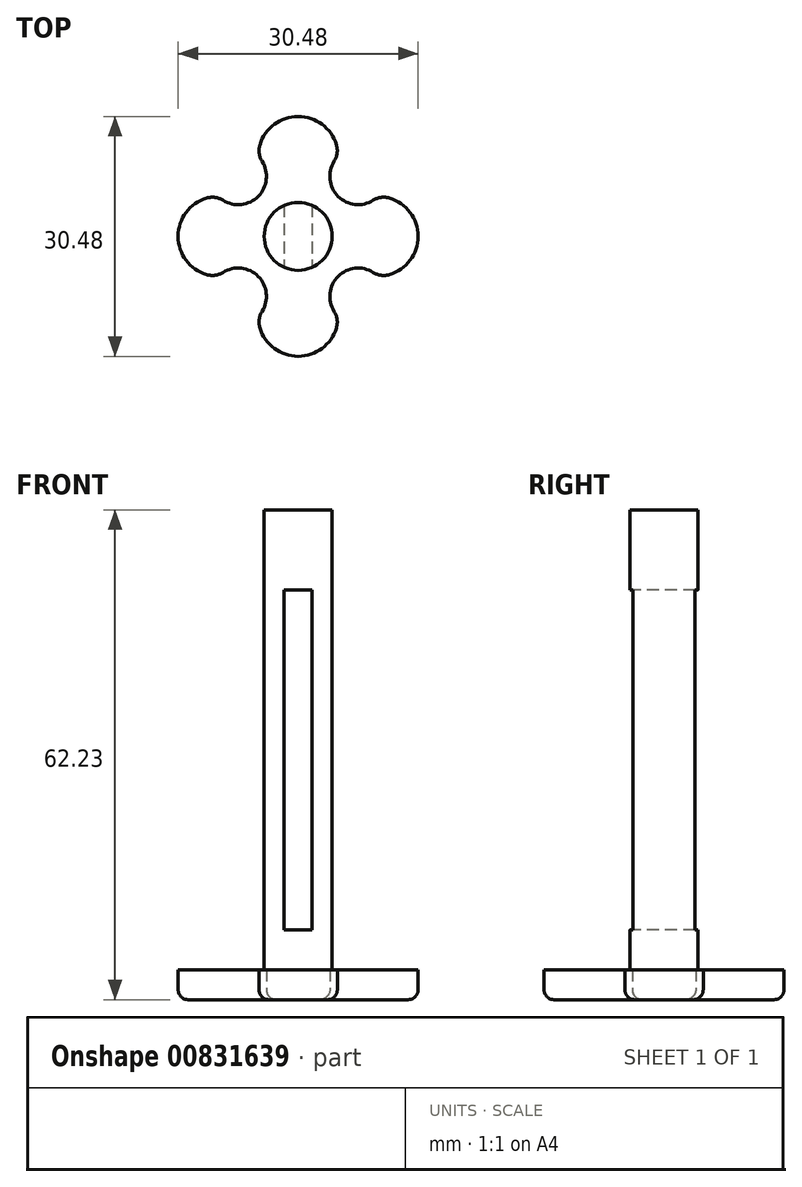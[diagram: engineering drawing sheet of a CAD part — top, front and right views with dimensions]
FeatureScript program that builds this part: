
annotation { "Feature Type Name" : "Feature", "Feature Type Description" : "" }
export const myFeature = defineFeature(function(context is Context, id is Id, definition is map)
    precondition{}
    {
        {
            var Q0;
            Q0=qCreatedBy(makeId("Top.planeOp"),FACE);
            var sketch = newSketch(context, id + "F0", { "sketchPlane" : qUnion([Q0])});
            skArc(sketch, "E0", {"start": v(5.08, 10.16) * mm, "mid": v(0, 15.24) * mm, "end": v(-5.08, 10.16) * mm});
            skLineSegment(sketch, "E1", {"start": v(0, 14.9) * mm, "end": v(0, -12.6) * mm, "construction": true});
            skArc(sketch, "E2", {"start": v(5.08, 10.16) * mm, "mid": v(5.08, 5.08) * mm, "end": v(10.16, 5.08) * mm});
            skLineSegment(sketch, "E3.0", {"start": v(10.16, 5.08) * mm, "end": v(5.08, 10.16) * mm, "construction": true});
            skLineSegment(sketch, "E4", {"start": v(-7.19, -7.19) * mm, "end": v(7.26, 7.26) * mm, "construction": true});
            skLineSegment(sketch, "E5", {"start": v(-9.15, 9.15) * mm, "end": v(9.27, -9.27) * mm, "construction": true});
            skPoint(sketch, "E6", {"position": v(0, 0) * mm});
            skLineSegment(sketch, "E7", {"start": v(-16.53, 0) * mm, "end": v(16.65, 0) * mm, "construction": true});
            skLineSegment(sketch, "E8", {"start": v(-4.19, 19.43) * mm, "end": v(17.03, -1.8) * mm, "construction": true});
            skArc(sketch, "E9.1.0", {"start": v(10.16, -5.08) * mm, "mid": v(15.24, 0) * mm, "end": v(10.16, 5.08) * mm});
            skArc(sketch, "E9.1.1", {"start": v(10.16, -5.08) * mm, "mid": v(5.08, -5.08) * mm, "end": v(5.08, -10.16) * mm});
            skArc(sketch, "E9.2.0", {"start": v(-5.08, -10.16) * mm, "mid": v(0, -15.24) * mm, "end": v(5.08, -10.16) * mm});
            skArc(sketch, "E9.2.1", {"start": v(-5.08, -10.16) * mm, "mid": v(-5.08, -5.08) * mm, "end": v(-10.16, -5.08) * mm});
            skArc(sketch, "E9.3.0", {"start": v(-10.16, 5.08) * mm, "mid": v(-15.24, 0) * mm, "end": v(-10.16, -5.08) * mm});
            skArc(sketch, "E9.3.1", {"start": v(-10.16, 5.08) * mm, "mid": v(-5.08, 5.08) * mm, "end": v(-5.08, 10.16) * mm});
            skLineSegment(sketch, "E9.anchor1", {"start": v(0, 0) * mm, "end": v(-5.08, 10.16) * mm, "construction": true});
            skLineSegment(sketch, "E9.anchor2", {"start": v(0, 0) * mm, "end": v(-10.16, -5.08) * mm, "construction": true});
            skCircle(sketch, "E10", {"center": v(0, 0) * mm, "radius": 4.32 * mm});
            skSolve(sketch);
        }
        {
            var Q0;
            Q0=makeQuery(id+"F0.imprint","IMPRINT",FACE,{"disambiguationData":[TD([[makeQuery(id+"F0.imprint","IMPRINT",EDGE,{"derivedFrom":sQuery(id+"F0.wireOp",EDGE,"E0")}),1.0]])]});
            extrude(context, id + "F1", {"entities" : qUnion([Q0]), "depth" : 3.8 * mm, "offsetDistance" : 25.4 * mm});
        }
        {
            var Q0;
            Q0=makeQuery(id+"F0.imprint","IMPRINT",FACE,{"disambiguationData":[TD([[makeQuery(id+"F0.imprint","IMPRINT",EDGE,{"derivedFrom":sQuery(id+"F0.wireOp",EDGE,"E10")}),1.0]])]});
            extrude(context, id + "F2", {"entities" : qUnion([Q0]), "operationType" : NewBodyOperationType.ADD, "depth" : 52.07 * mm, "offsetDistance" : 25.4 * mm});
        }
        {
            var Q0;
            Q0=makeQuery(id+"F2.opExtrude","CAP_FACE",FACE,{"disambiguationData":[OSD([sQuery(id+"F0.wireOp",EDGE,"E10")])],"isStart":false});
            var sketch = newSketch(context, id + "F3", { "sketchPlane" : qUnion([Q0])});
            skLineSegment(sketch, "E11.bottom", {"start": v(1.78, 4.61) * mm, "end": v(-1.78, 4.61) * mm});
            skLineSegment(sketch, "E11.top", {"start": v(1.78, -4.61) * mm, "end": v(-1.78, -4.61) * mm});
            skLineSegment(sketch, "E11.left", {"start": v(1.78, 4.61) * mm, "end": v(1.78, -4.61) * mm});
            skLineSegment(sketch, "E11.right", {"start": v(-1.78, 4.61) * mm, "end": v(-1.78, -4.61) * mm});
            skPoint(sketch, "E11.middle", {"position": v(0, 0) * mm});
            skSolve(sketch);
        }
        {
            var Q0;
            {var subQ0=sQuery(id+"F3.wireOp",EDGE,"E11.left");var subQ1=makeQuery(id+"F2.opExtrude","CAP_EDGE",EDGE,{"disambiguationData":[OSD([sQuery(id+"F0.wireOp",EDGE,"E10")])],"isStart":false});var subQ2=makeQuery(id+"F3.imprint","INTERSECT",VERTEX,{"disambiguationData":[OD(0.0)],"derivedFrom":[subQ1,subQ0]});Q0=makeQuery(id+"F3.imprint","IMPRINT",FACE,{"disambiguationData":[TD([[makeQuery(id+"F3.imprint","IMPRINT",EDGE,{"disambiguationData":[TD([[subQ2,-1.0]])],"derivedFrom":subQ0}),-1.0]])]});}
            extrude(context, id + "F4", {"entities" : qUnion([Q0]), "operationType" : NewBodyOperationType.REMOVE, "oppositeDirection" : true, "depth" : 43.18 * mm, "offsetDistance" : 25.4 * mm});
        }
        {
            var Q0;
            {var subQ0=sQuery(id+"F0.wireOp",EDGE,"E10");Q0=makeQuery(id+"F4.boolean.opBoolean","SPLIT",FACE,{"disambiguationData":[TD([makeQuery(id+"F4.opExtrude","SWEPT_FACE",FACE,{"disambiguationData":[OSD([sQuery(id+"F3.wireOp",EDGE,"E11.left")])]})])],"derivedFrom":makeQuery(id+"F2.opExtrude","CAP_FACE",FACE,{"disambiguationData":[OSD([subQ0])],"isStart":false})});}
            var sketch = newSketch(context, id + "F5", { "sketchPlane" : qUnion([Q0])});
            skCircle(sketch, "E12", {"center": v(0, 0) * mm, "radius": 4.32 * mm});
            skSolve(sketch);
        }
        {
            var Q0;
            {var subQ1=makeQuery(id+"F4.boolean.opBoolean","COPY",EDGE,{"derivedFrom":makeQuery(id+"F4.opExtrude","CAP_EDGE",EDGE,{"disambiguationData":[OSD([sQuery(id+"F3.wireOp",EDGE,"E11.left")])],"isStart":true})});Q0=makeQuery(id+"F5.imprint","IMPRINT",FACE,{"disambiguationData":[TD([[makeQuery(id+"F5.imprint","IMPRINT",EDGE,{"derivedFrom":subQ1}),-1.0]])]});}
            var Q1;
            {var subQ1=makeQuery(id+"F4.boolean.opBoolean","COPY",EDGE,{"derivedFrom":makeQuery(id+"F4.opExtrude","CAP_EDGE",EDGE,{"disambiguationData":[OSD([sQuery(id+"F3.wireOp",EDGE,"E11.left")])],"isStart":true})});Q1=makeQuery(id+"F5.imprint","IMPRINT",FACE,{"disambiguationData":[TD([[makeQuery(id+"F5.imprint","IMPRINT",EDGE,{"derivedFrom":subQ1}),1.0]])]});}
            extrude(context, id + "F6", {"entities" : qUnion([Q0, Q1]), "operationType" : NewBodyOperationType.ADD, "depth" : 10.16 * mm, "offsetDistance" : 25.4 * mm});
        }
        {
            var Q0;
            Q0=makeQuery(id+"F1.opExtrude","SWEPT_EDGE",EDGE,{"disambiguationData":[OSD([sQuery(id+"F0.wireOp",EDGE,"E9.2.0"),sQuery(id+"F0.wireOp",EDGE,"E9.2.1")])]});
            var Q1;
            Q1=makeQuery(id+"F1.opExtrude","SWEPT_EDGE",EDGE,{"disambiguationData":[OSD([sQuery(id+"F0.wireOp",EDGE,"E9.2.1"),sQuery(id+"F0.wireOp",EDGE,"E9.3.0")])]});
            var Q2;
            Q2=makeQuery(id+"F1.opExtrude","SWEPT_EDGE",EDGE,{"disambiguationData":[OSD([sQuery(id+"F0.wireOp",EDGE,"E9.1.1"),sQuery(id+"F0.wireOp",EDGE,"E9.2.0")])]});
            var Q3;
            Q3=makeQuery(id+"F1.opExtrude","SWEPT_EDGE",EDGE,{"disambiguationData":[OSD([sQuery(id+"F0.wireOp",EDGE,"E9.1.0"),sQuery(id+"F0.wireOp",EDGE,"E9.1.1")])]});
            var Q4;
            Q4=makeQuery(id+"F1.opExtrude","SWEPT_EDGE",EDGE,{"disambiguationData":[OSD([sQuery(id+"F0.wireOp",EDGE,"E2"),sQuery(id+"F0.wireOp",EDGE,"E9.1.0")])]});
            var Q5;
            Q5=makeQuery(id+"F1.opExtrude","SWEPT_EDGE",EDGE,{"disambiguationData":[OSD([sQuery(id+"F0.wireOp",EDGE,"E0"),sQuery(id+"F0.wireOp",EDGE,"E2")])]});
            var Q6;
            Q6=makeQuery(id+"F1.opExtrude","SWEPT_EDGE",EDGE,{"disambiguationData":[OSD([sQuery(id+"F0.wireOp",EDGE,"E9.3.0"),sQuery(id+"F0.wireOp",EDGE,"E9.3.1")])]});
            var Q7;
            Q7=makeQuery(id+"F1.opExtrude","SWEPT_EDGE",EDGE,{"disambiguationData":[OSD([sQuery(id+"F0.wireOp",EDGE,"E0"),sQuery(id+"F0.wireOp",EDGE,"E9.3.1")])]});
            fillet(context, id + "F7", {"entities" : qUnion([Q0, Q1, Q2, Q3, Q4, Q5, Q6, Q7]), "radius" : 2.54 * mm, "tangentPropagation" : true, "allowEdgeOverflow" : false});
        }
        {
            var Q0;
            Q0=makeQuery(id+"F1.opExtrude","CAP_EDGE",EDGE,{"disambiguationData":[OSD([sQuery(id+"F0.wireOp",EDGE,"E9.3.0")])],"isStart":true});
            var Q1;
            Q1=makeQuery(id+"F1.opExtrude","CAP_EDGE",EDGE,{"disambiguationData":[OSD([sQuery(id+"F0.wireOp",EDGE,"E9.2.1")])],"isStart":true});
            var Q2;
            Q2=makeQuery(id+"F1.opExtrude","CAP_EDGE",EDGE,{"disambiguationData":[OSD([sQuery(id+"F0.wireOp",EDGE,"E9.2.0")])],"isStart":true});
            var Q3;
            {var subQ0=sQuery(id+"F0.wireOp",EDGE,"E10");var subQ1=sQuery(id+"F0.wireOp",EDGE,"E9.3.0");var subQ2=sQuery(id+"F0.wireOp",EDGE,"E9.2.1");Q3=makeQuery(id+"F7.opFillet","BLEND_EDGE",EDGE,{"blendedFrom":[makeQuery(id+"F1.opExtrude","SWEPT_EDGE",EDGE,{"disambiguationData":[OSD([subQ2,subQ1])]}),makeQuery(id+"F2.boolean.opBoolean","MERGE",FACE,{"derivedFrom":[makeQuery(id+"F1.opExtrude","CAP_FACE",FACE,{"disambiguationData":[OSD([sQuery(id+"F0.wireOp",EDGE,"E0"),sQuery(id+"F0.wireOp",EDGE,"E2"),sQuery(id+"F0.wireOp",EDGE,"E9.1.0"),sQuery(id+"F0.wireOp",EDGE,"E9.1.1"),sQuery(id+"F0.wireOp",EDGE,"E9.2.0"),subQ2,subQ1,sQuery(id+"F0.wireOp",EDGE,"E9.3.1"),subQ0])],"isStart":true}),makeQuery(id+"F2.opExtrude","CAP_FACE",FACE,{"disambiguationData":[OSD([subQ0])],"isStart":true})]})],"blendedInto":[makeQuery(id+"F2.boolean.opBoolean","MERGE",FACE,{"derivedFrom":[makeQuery(id+"F1.opExtrude","CAP_FACE",FACE,{"disambiguationData":[OSD([sQuery(id+"F0.wireOp",EDGE,"E0"),sQuery(id+"F0.wireOp",EDGE,"E2"),sQuery(id+"F0.wireOp",EDGE,"E9.1.0"),sQuery(id+"F0.wireOp",EDGE,"E9.1.1"),sQuery(id+"F0.wireOp",EDGE,"E9.2.0"),subQ2,subQ1,sQuery(id+"F0.wireOp",EDGE,"E9.3.1"),subQ0])],"isStart":true}),makeQuery(id+"F2.opExtrude","CAP_FACE",FACE,{"disambiguationData":[OSD([subQ0])],"isStart":true})]})]});}
            var Q4;
            Q4=makeQuery(id+"F1.opExtrude","CAP_EDGE",EDGE,{"disambiguationData":[OSD([sQuery(id+"F0.wireOp",EDGE,"E9.1.1")])],"isStart":true});
            var Q5;
            {var subQ0=sQuery(id+"F0.wireOp",EDGE,"E10");var subQ1=sQuery(id+"F0.wireOp",EDGE,"E9.2.0");var subQ2=sQuery(id+"F0.wireOp",EDGE,"E9.1.1");Q5=makeQuery(id+"F7.opFillet","BLEND_EDGE",EDGE,{"blendedFrom":[makeQuery(id+"F1.opExtrude","SWEPT_EDGE",EDGE,{"disambiguationData":[OSD([subQ2,subQ1])]}),makeQuery(id+"F2.boolean.opBoolean","MERGE",FACE,{"derivedFrom":[makeQuery(id+"F1.opExtrude","CAP_FACE",FACE,{"disambiguationData":[OSD([sQuery(id+"F0.wireOp",EDGE,"E0"),sQuery(id+"F0.wireOp",EDGE,"E2"),sQuery(id+"F0.wireOp",EDGE,"E9.1.0"),subQ2,subQ1,sQuery(id+"F0.wireOp",EDGE,"E9.2.1"),sQuery(id+"F0.wireOp",EDGE,"E9.3.0"),sQuery(id+"F0.wireOp",EDGE,"E9.3.1"),subQ0])],"isStart":true}),makeQuery(id+"F2.opExtrude","CAP_FACE",FACE,{"disambiguationData":[OSD([subQ0])],"isStart":true})]})],"blendedInto":[makeQuery(id+"F2.boolean.opBoolean","MERGE",FACE,{"derivedFrom":[makeQuery(id+"F1.opExtrude","CAP_FACE",FACE,{"disambiguationData":[OSD([sQuery(id+"F0.wireOp",EDGE,"E0"),sQuery(id+"F0.wireOp",EDGE,"E2"),sQuery(id+"F0.wireOp",EDGE,"E9.1.0"),subQ2,subQ1,sQuery(id+"F0.wireOp",EDGE,"E9.2.1"),sQuery(id+"F0.wireOp",EDGE,"E9.3.0"),sQuery(id+"F0.wireOp",EDGE,"E9.3.1"),subQ0])],"isStart":true}),makeQuery(id+"F2.opExtrude","CAP_FACE",FACE,{"disambiguationData":[OSD([subQ0])],"isStart":true})]})]});}
            var Q6;
            {var subQ0=sQuery(id+"F0.wireOp",EDGE,"E10");var subQ1=sQuery(id+"F0.wireOp",EDGE,"E9.1.1");var subQ2=sQuery(id+"F0.wireOp",EDGE,"E9.1.0");Q6=makeQuery(id+"F7.opFillet","BLEND_EDGE",EDGE,{"blendedFrom":[makeQuery(id+"F1.opExtrude","SWEPT_EDGE",EDGE,{"disambiguationData":[OSD([subQ2,subQ1])]}),makeQuery(id+"F2.boolean.opBoolean","MERGE",FACE,{"derivedFrom":[makeQuery(id+"F1.opExtrude","CAP_FACE",FACE,{"disambiguationData":[OSD([sQuery(id+"F0.wireOp",EDGE,"E0"),sQuery(id+"F0.wireOp",EDGE,"E2"),subQ2,subQ1,sQuery(id+"F0.wireOp",EDGE,"E9.2.0"),sQuery(id+"F0.wireOp",EDGE,"E9.2.1"),sQuery(id+"F0.wireOp",EDGE,"E9.3.0"),sQuery(id+"F0.wireOp",EDGE,"E9.3.1"),subQ0])],"isStart":true}),makeQuery(id+"F2.opExtrude","CAP_FACE",FACE,{"disambiguationData":[OSD([subQ0])],"isStart":true})]})],"blendedInto":[makeQuery(id+"F2.boolean.opBoolean","MERGE",FACE,{"derivedFrom":[makeQuery(id+"F1.opExtrude","CAP_FACE",FACE,{"disambiguationData":[OSD([sQuery(id+"F0.wireOp",EDGE,"E0"),sQuery(id+"F0.wireOp",EDGE,"E2"),subQ2,subQ1,sQuery(id+"F0.wireOp",EDGE,"E9.2.0"),sQuery(id+"F0.wireOp",EDGE,"E9.2.1"),sQuery(id+"F0.wireOp",EDGE,"E9.3.0"),sQuery(id+"F0.wireOp",EDGE,"E9.3.1"),subQ0])],"isStart":true}),makeQuery(id+"F2.opExtrude","CAP_FACE",FACE,{"disambiguationData":[OSD([subQ0])],"isStart":true})]})]});}
            var Q7;
            Q7=makeQuery(id+"F1.opExtrude","CAP_EDGE",EDGE,{"disambiguationData":[OSD([sQuery(id+"F0.wireOp",EDGE,"E9.1.0")])],"isStart":true});
            var Q8;
            {var subQ0=sQuery(id+"F0.wireOp",EDGE,"E10");var subQ1=sQuery(id+"F0.wireOp",EDGE,"E9.1.0");var subQ2=sQuery(id+"F0.wireOp",EDGE,"E2");Q8=makeQuery(id+"F7.opFillet","BLEND_EDGE",EDGE,{"blendedFrom":[makeQuery(id+"F1.opExtrude","SWEPT_EDGE",EDGE,{"disambiguationData":[OSD([subQ2,subQ1])]}),makeQuery(id+"F2.boolean.opBoolean","MERGE",FACE,{"derivedFrom":[makeQuery(id+"F1.opExtrude","CAP_FACE",FACE,{"disambiguationData":[OSD([sQuery(id+"F0.wireOp",EDGE,"E0"),subQ2,subQ1,sQuery(id+"F0.wireOp",EDGE,"E9.1.1"),sQuery(id+"F0.wireOp",EDGE,"E9.2.0"),sQuery(id+"F0.wireOp",EDGE,"E9.2.1"),sQuery(id+"F0.wireOp",EDGE,"E9.3.0"),sQuery(id+"F0.wireOp",EDGE,"E9.3.1"),subQ0])],"isStart":true}),makeQuery(id+"F2.opExtrude","CAP_FACE",FACE,{"disambiguationData":[OSD([subQ0])],"isStart":true})]})],"blendedInto":[makeQuery(id+"F2.boolean.opBoolean","MERGE",FACE,{"derivedFrom":[makeQuery(id+"F1.opExtrude","CAP_FACE",FACE,{"disambiguationData":[OSD([sQuery(id+"F0.wireOp",EDGE,"E0"),subQ2,subQ1,sQuery(id+"F0.wireOp",EDGE,"E9.1.1"),sQuery(id+"F0.wireOp",EDGE,"E9.2.0"),sQuery(id+"F0.wireOp",EDGE,"E9.2.1"),sQuery(id+"F0.wireOp",EDGE,"E9.3.0"),sQuery(id+"F0.wireOp",EDGE,"E9.3.1"),subQ0])],"isStart":true}),makeQuery(id+"F2.opExtrude","CAP_FACE",FACE,{"disambiguationData":[OSD([subQ0])],"isStart":true})]})]});}
            var Q9;
            Q9=makeQuery(id+"F1.opExtrude","CAP_EDGE",EDGE,{"disambiguationData":[OSD([sQuery(id+"F0.wireOp",EDGE,"E2")])],"isStart":true});
            var Q10;
            {var subQ0=sQuery(id+"F0.wireOp",EDGE,"E10");var subQ1=sQuery(id+"F0.wireOp",EDGE,"E2");var subQ2=sQuery(id+"F0.wireOp",EDGE,"E0");Q10=makeQuery(id+"F7.opFillet","BLEND_EDGE",EDGE,{"blendedFrom":[makeQuery(id+"F1.opExtrude","SWEPT_EDGE",EDGE,{"disambiguationData":[OSD([subQ2,subQ1])]}),makeQuery(id+"F2.boolean.opBoolean","MERGE",FACE,{"derivedFrom":[makeQuery(id+"F1.opExtrude","CAP_FACE",FACE,{"disambiguationData":[OSD([subQ2,subQ1,sQuery(id+"F0.wireOp",EDGE,"E9.1.0"),sQuery(id+"F0.wireOp",EDGE,"E9.1.1"),sQuery(id+"F0.wireOp",EDGE,"E9.2.0"),sQuery(id+"F0.wireOp",EDGE,"E9.2.1"),sQuery(id+"F0.wireOp",EDGE,"E9.3.0"),sQuery(id+"F0.wireOp",EDGE,"E9.3.1"),subQ0])],"isStart":true}),makeQuery(id+"F2.opExtrude","CAP_FACE",FACE,{"disambiguationData":[OSD([subQ0])],"isStart":true})]})],"blendedInto":[makeQuery(id+"F2.boolean.opBoolean","MERGE",FACE,{"derivedFrom":[makeQuery(id+"F1.opExtrude","CAP_FACE",FACE,{"disambiguationData":[OSD([subQ2,subQ1,sQuery(id+"F0.wireOp",EDGE,"E9.1.0"),sQuery(id+"F0.wireOp",EDGE,"E9.1.1"),sQuery(id+"F0.wireOp",EDGE,"E9.2.0"),sQuery(id+"F0.wireOp",EDGE,"E9.2.1"),sQuery(id+"F0.wireOp",EDGE,"E9.3.0"),sQuery(id+"F0.wireOp",EDGE,"E9.3.1"),subQ0])],"isStart":true}),makeQuery(id+"F2.opExtrude","CAP_FACE",FACE,{"disambiguationData":[OSD([subQ0])],"isStart":true})]})]});}
            var Q11;
            Q11=makeQuery(id+"F1.opExtrude","CAP_EDGE",EDGE,{"disambiguationData":[OSD([sQuery(id+"F0.wireOp",EDGE,"E0")])],"isStart":true});
            var Q12;
            {var subQ0=sQuery(id+"F0.wireOp",EDGE,"E10");var subQ1=sQuery(id+"F0.wireOp",EDGE,"E9.3.1");var subQ2=sQuery(id+"F0.wireOp",EDGE,"E0");Q12=makeQuery(id+"F7.opFillet","BLEND_EDGE",EDGE,{"blendedFrom":[makeQuery(id+"F1.opExtrude","SWEPT_EDGE",EDGE,{"disambiguationData":[OSD([subQ2,subQ1])]}),makeQuery(id+"F2.boolean.opBoolean","MERGE",FACE,{"derivedFrom":[makeQuery(id+"F1.opExtrude","CAP_FACE",FACE,{"disambiguationData":[OSD([subQ2,sQuery(id+"F0.wireOp",EDGE,"E2"),sQuery(id+"F0.wireOp",EDGE,"E9.1.0"),sQuery(id+"F0.wireOp",EDGE,"E9.1.1"),sQuery(id+"F0.wireOp",EDGE,"E9.2.0"),sQuery(id+"F0.wireOp",EDGE,"E9.2.1"),sQuery(id+"F0.wireOp",EDGE,"E9.3.0"),subQ1,subQ0])],"isStart":true}),makeQuery(id+"F2.opExtrude","CAP_FACE",FACE,{"disambiguationData":[OSD([subQ0])],"isStart":true})]})],"blendedInto":[makeQuery(id+"F2.boolean.opBoolean","MERGE",FACE,{"derivedFrom":[makeQuery(id+"F1.opExtrude","CAP_FACE",FACE,{"disambiguationData":[OSD([subQ2,sQuery(id+"F0.wireOp",EDGE,"E2"),sQuery(id+"F0.wireOp",EDGE,"E9.1.0"),sQuery(id+"F0.wireOp",EDGE,"E9.1.1"),sQuery(id+"F0.wireOp",EDGE,"E9.2.0"),sQuery(id+"F0.wireOp",EDGE,"E9.2.1"),sQuery(id+"F0.wireOp",EDGE,"E9.3.0"),subQ1,subQ0])],"isStart":true}),makeQuery(id+"F2.opExtrude","CAP_FACE",FACE,{"disambiguationData":[OSD([subQ0])],"isStart":true})]})]});}
            var Q13;
            Q13=makeQuery(id+"F1.opExtrude","CAP_EDGE",EDGE,{"disambiguationData":[OSD([sQuery(id+"F0.wireOp",EDGE,"E9.3.1")])],"isStart":true});
            var Q14;
            {var subQ0=sQuery(id+"F0.wireOp",EDGE,"E10");Q14=makeQuery(id+"F2.boolean.opBoolean","MERGE",FACE,{"derivedFrom":[makeQuery(id+"F1.opExtrude","CAP_FACE",FACE,{"disambiguationData":[OSD([sQuery(id+"F0.wireOp",EDGE,"E0"),sQuery(id+"F0.wireOp",EDGE,"E2"),sQuery(id+"F0.wireOp",EDGE,"E9.1.0"),sQuery(id+"F0.wireOp",EDGE,"E9.1.1"),sQuery(id+"F0.wireOp",EDGE,"E9.2.0"),sQuery(id+"F0.wireOp",EDGE,"E9.2.1"),sQuery(id+"F0.wireOp",EDGE,"E9.3.0"),sQuery(id+"F0.wireOp",EDGE,"E9.3.1"),subQ0])],"isStart":true}),makeQuery(id+"F2.opExtrude","CAP_FACE",FACE,{"disambiguationData":[OSD([subQ0])],"isStart":true})]});}
            fillet(context, id + "F8", {"entities" : qUnion([Q0, Q1, Q2, Q3, Q4, Q5, Q6, Q7, Q8, Q9, Q10, Q11, Q12, Q13, Q14]), "radius" : 1.27 * mm, "tangentPropagation" : true, "allowEdgeOverflow" : false});
        }
    });
